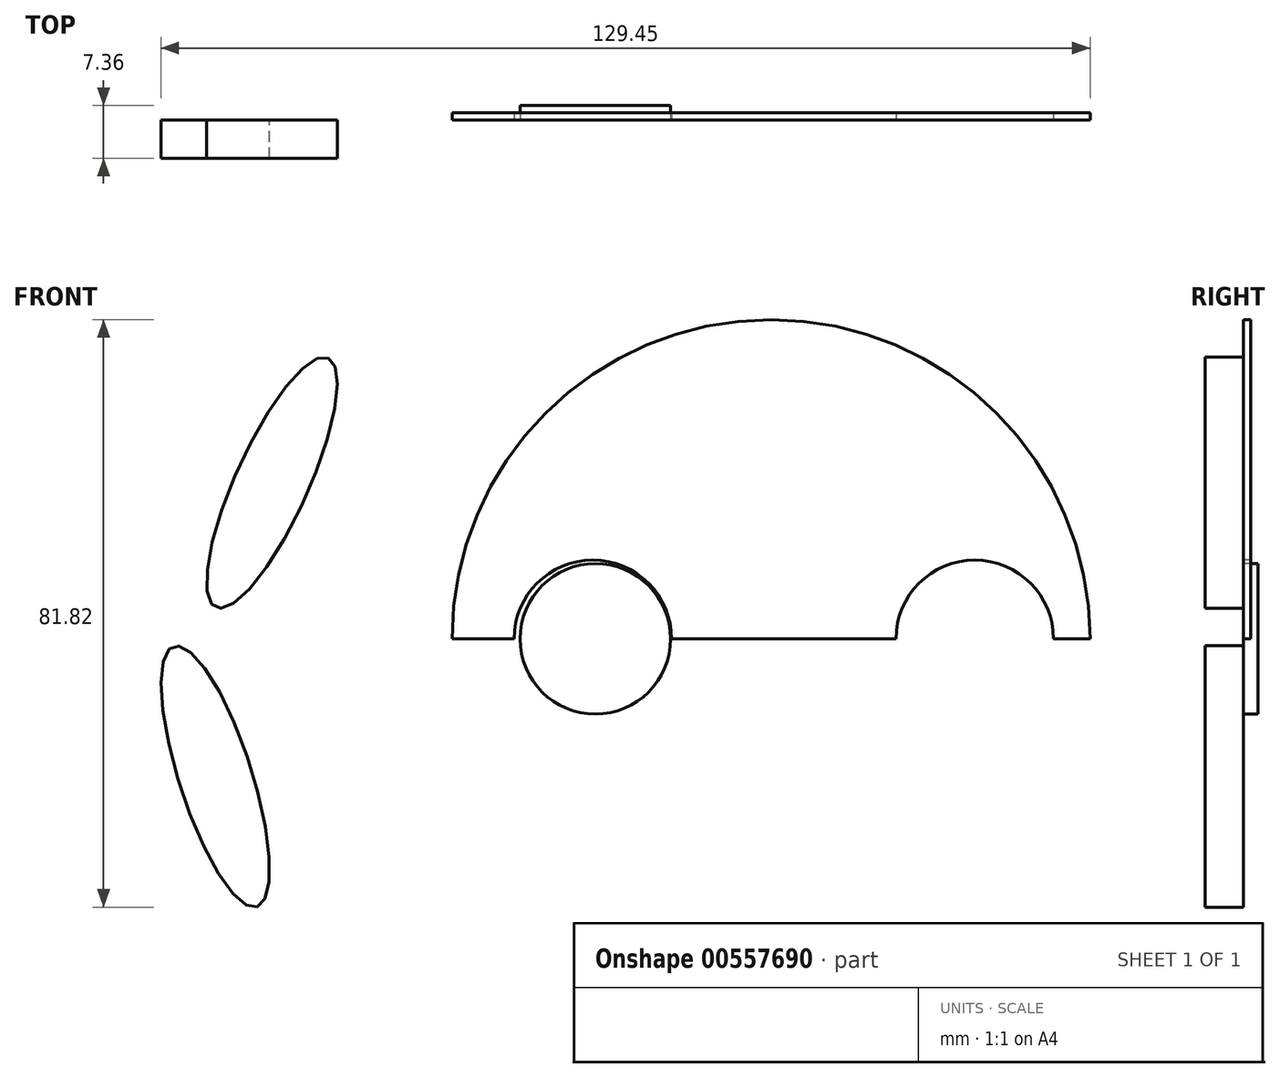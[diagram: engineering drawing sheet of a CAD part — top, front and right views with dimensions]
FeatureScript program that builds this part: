
annotation { "Feature Type Name" : "Feature", "Feature Type Description" : "" }
export const myFeature = defineFeature(function(context is Context, id is Id, definition is map)
    precondition{}
    {
        {
            var Q0;
            Q0=qCreatedBy(makeId("Front.planeOp"),FACE);
            var sketch = newSketch(context, id + "F0", { "sketchPlane" : qUnion([Q0])});
            skArc(sketch, "E0", {"start": v(44.54, 0) * mm, "mid": v(0.09, 44.45) * mm, "end": v(-44.36, 0) * mm});
            skLineSegment(sketch, "E1", {"start": v(-44.36, 0) * mm, "end": v(44.54, 0) * mm});
            skCircle(sketch, "E2", {"center": v(28.47, 0) * mm, "radius": 10.97 * mm});
            skCircle(sketch, "E3", {"center": v(28.47, 0) * mm, "radius": 6.35 * mm});
            skCircle(sketch, "E4", {"center": v(-24.75, 0) * mm, "radius": 10.97 * mm});
            skCircle(sketch, "E5", {"center": v(-24.75, 0) * mm, "radius": 6.35 * mm});
            skSolve(sketch);
        }
        {
            var Q0;
            Q0=sQuery(id+"F0.wireOp",EDGE,"E0");
            extrude(context, id + "F1", {"bodyType" : ToolBodyType.SURFACE, "surfaceEntities" : qUnion([Q0]), "oppositeDirection" : true, "depth" : 2.8 * mm, "offsetDistance" : 25.4 * mm});
        }
        {
            var Q0;
            Q0=sQuery(id+"F0.wireOp",EDGE,"E4");
            var Q1;
            Q1=sQuery(id+"F0.wireOp",EDGE,"E5");
            extrude(context, id + "F2", {"bodyType" : ToolBodyType.SURFACE, "surfaceEntities" : qUnion([Q0, Q1]), "oppositeDirection" : true, "depth" : 3.56 * mm, "offsetDistance" : 25.4 * mm});
        }
        {
            var Q0;
            {var subQ1=sQuery(id+"F0.wireOp",EDGE,"E0");Q0=makeQuery(id+"F0.imprint","IMPRINT",FACE,{"disambiguationData":[TD([[makeQuery(id+"F0.imprint","IMPRINT",EDGE,{"derivedFrom":subQ1}),1.0]])]});}
            extrude(context, id + "F3", {"entities" : qUnion([Q0]), "oppositeDirection" : true, "depth" : 1.02 * mm, "offsetDistance" : 25.4 * mm});
        }
        {
            var Q0;
            Q0=sQuery(id+"F0.wireOp",EDGE,"E2");
            var Q1;
            Q1=sQuery(id+"F0.wireOp",EDGE,"E3");
            extrude(context, id + "F4", {"bodyType" : ToolBodyType.SURFACE, "surfaceEntities" : qUnion([Q0, Q1]), "oppositeDirection" : true, "depth" : 3.56 * mm, "offsetDistance" : 25.4 * mm});
        }
        {
            var Q0;
            Q0=makeQuery(id+"F3.opExtrude","CAP_FACE",FACE,{"disambiguationData":[OSD([sQuery(id+"F0.wireOp",EDGE,"E0"),sQuery(id+"F0.wireOp",EDGE,"E1"),sQuery(id+"F0.wireOp",EDGE,"E2"),sQuery(id+"F0.wireOp",EDGE,"E4")])],"isStart":false});
            var sketch = newSketch(context, id + "F5", { "sketchPlane" : qUnion([Q0])});
            skLineSegment(sketch, "E6", {"start": v(44.36, 0) * mm, "end": v(68.84, 22.17) * mm});
            skLineSegment(sketch, "E7", {"start": v(44.36, 0) * mm, "end": v(72.94, -16.55) * mm});
            skSolve(sketch);
        }
        {
            var Q0;
            Q0=sQuery(id+"F5.wireOp",EDGE,"E6");
            var Q1;
            Q1=sQuery(id+"F5.wireOp",EDGE,"E7");
            extrude(context, id + "F6", {"bodyType" : ToolBodyType.SURFACE, "surfaceEntities" : qUnion([Q0, Q1]), "oppositeDirection" : true, "depth" : 3.56 * mm, "offsetDistance" : 25.4 * mm});
        }
        {
            var Q0;
            Q0=qCreatedBy(makeId("Front.planeOp"),FACE);
            var sketch = newSketch(context, id + "F7", { "sketchPlane" : qUnion([Q0])});
            skEllipse(sketch, "E8", {"center": v(-69.46, 21.75) * mm, "majorRadius": 19.05 * mm, "minorRadius": 5.08 * mm, "majorAxis": v(0.41, 0.91)});
            skEllipse(sketch, "E9", {"center": v(-77.35, -19.16) * mm, "majorRadius": 19.05 * mm, "minorRadius": 5.08 * mm, "majorAxis": v(0.3, -0.95)});
            skSolve(sketch);
        }
        {
            var Q0;
            Q0=makeQuery(id+"F7.imprint","IMPRINT",FACE,{"disambiguationData":[TD([[makeQuery(id+"F7.imprint","IMPRINT",EDGE,{"derivedFrom":sQuery(id+"F7.wireOp",EDGE,"E9")}),1.0]])]});
            var Q1;
            Q1=makeQuery(id+"F7.imprint","IMPRINT",FACE,{"disambiguationData":[TD([[makeQuery(id+"F7.imprint","IMPRINT",EDGE,{"derivedFrom":sQuery(id+"F7.wireOp",EDGE,"E8")}),1.0]])]});
            extrude(context, id + "F8", {"entities" : qUnion([Q0, Q1]), "depth" : 5.33 * mm, "offsetDistance" : 25.4 * mm});
        }
        {
            var Q0;
            Q0=qCreatedBy(makeId("Front.planeOp"),FACE);
            var sketch = newSketch(context, id + "F9", { "sketchPlane" : qUnion([Q0])});
            skCircle(sketch, "E10", {"center": v(-24.4, 0) * mm, "radius": 10.49 * mm});
            skSolve(sketch);
        }
        {
            var Q0;
            Q0 = qSketchRegion(id + "F9", true);
            extrude(context, id + "F10", {"entities" : qUnion([Q0]), "oppositeDirection" : true, "depth" : 2.03 * mm, "offsetDistance" : 25.4 * mm});
        }
    });
